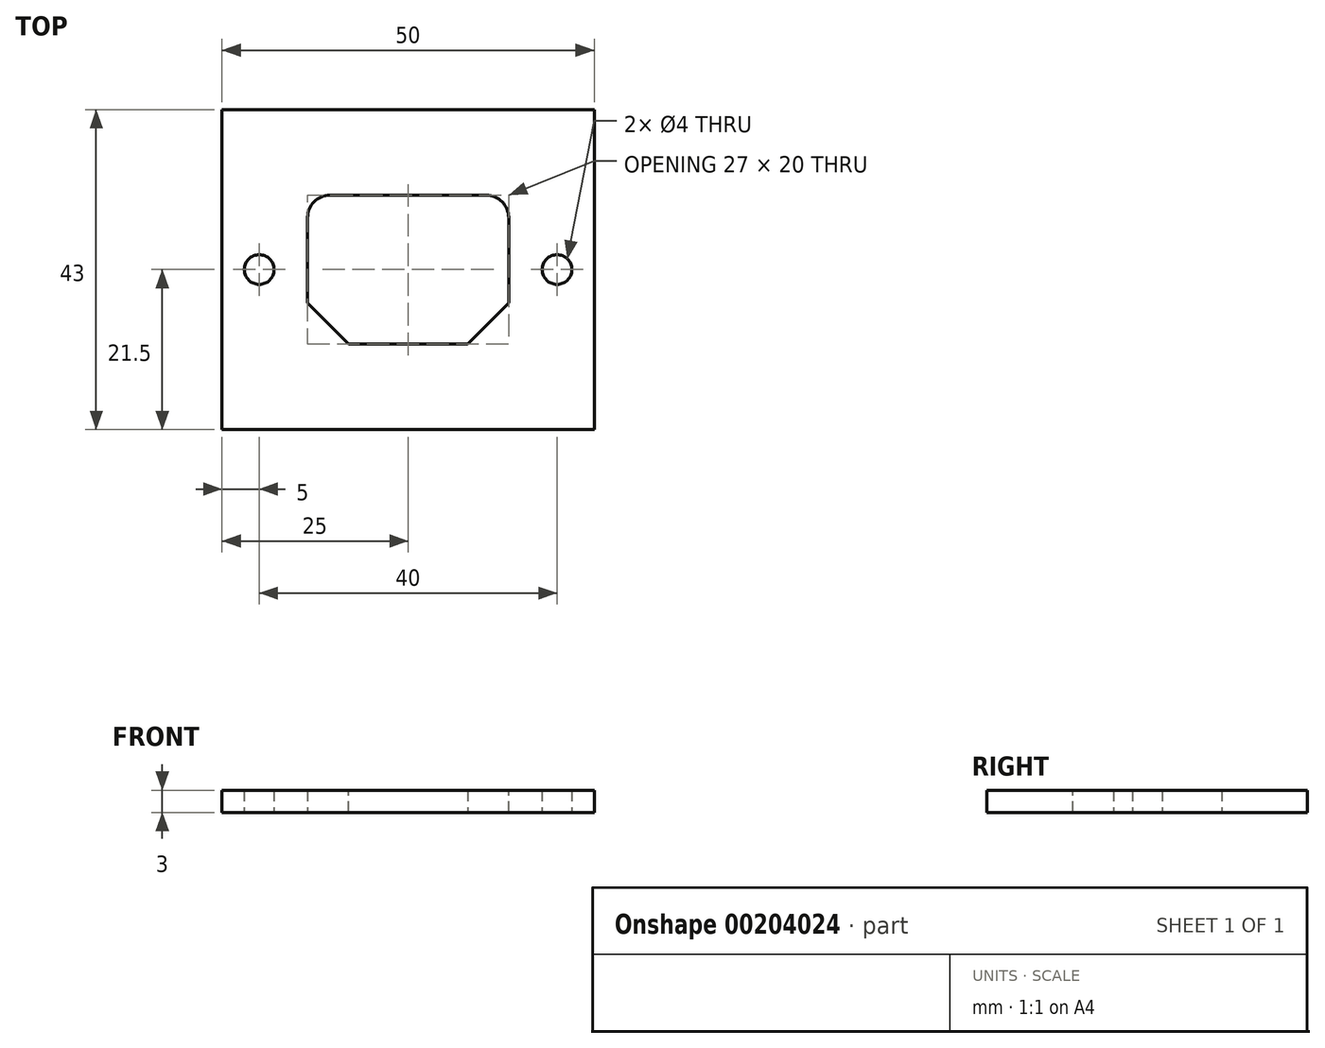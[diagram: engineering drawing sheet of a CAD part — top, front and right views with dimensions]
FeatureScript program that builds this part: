
annotation { "Feature Type Name" : "Feature", "Feature Type Description" : "" }
export const myFeature = defineFeature(function(context is Context, id is Id, definition is map)
    precondition{}
    {
        {
            var Q0;
            Q0=qCreatedBy(makeId("Top.planeOp"),FACE);
            var sketch = newSketch(context, id + "F0", { "sketchPlane" : qUnion([Q0])});
            skLineSegment(sketch, "E0", {"start": v(-13.5, -10) * mm, "end": v(13.5, -10) * mm});
            skLineSegment(sketch, "E1", {"start": v(13.5, -10) * mm, "end": v(13.5, 10) * mm});
            skLineSegment(sketch, "E2", {"start": v(13.5, 10) * mm, "end": v(-13.5, 10) * mm});
            skLineSegment(sketch, "E3", {"start": v(-13.5, 10) * mm, "end": v(-13.5, -10) * mm});
            skLineSegment(sketch, "E4.0", {"start": v(25, 21.5) * mm, "end": v(-25, 21.5) * mm});
            skLineSegment(sketch, "E4.1", {"start": v(25, -21.5) * mm, "end": v(25, 21.5) * mm});
            skLineSegment(sketch, "E4.2", {"start": v(-25, -21.5) * mm, "end": v(25, -21.5) * mm});
            skLineSegment(sketch, "E4.3", {"start": v(-25, 21.5) * mm, "end": v(-25, -21.5) * mm});
            skCircle(sketch, "E5", {"center": v(-20, 0) * mm, "radius": 2 * mm});
            skCircle(sketch, "E6", {"center": v(20, 0) * mm, "radius": 2 * mm});
            skSolve(sketch);
        }
        {
            var Q0;
            Q0=makeQuery(id+"F0.imprint","IMPRINT",FACE,{"disambiguationData":[TD([[makeQuery(id+"F0.imprint","IMPRINT",EDGE,{"derivedFrom":sQuery(id+"F0.wireOp",EDGE,"E0")}),-1.0]])]});
            extrude(context, id + "F1", {"entities" : qUnion([Q0]), "depth" : 3 * mm});
        }
        {
            var Q0;
            Q0=makeQuery(id+"F1.opExtrude","SWEPT_EDGE",EDGE,{"disambiguationData":[OSD([sQuery(id+"F0.wireOp",EDGE,"E2"),sQuery(id+"F0.wireOp",EDGE,"E3")])]});
            var Q1;
            Q1=makeQuery(id+"F1.opExtrude","SWEPT_EDGE",EDGE,{"disambiguationData":[OSD([sQuery(id+"F0.wireOp",EDGE,"E1"),sQuery(id+"F0.wireOp",EDGE,"E2")])]});
            fillet(context, id + "F2", {"entities" : qUnion([Q0, Q1]), "radius" : 3 * mm, "tangentPropagation" : true, "allowEdgeOverflow" : false});
        }
        {
            var Q0;
            Q0=makeQuery(id+"F1.opExtrude","SWEPT_EDGE",EDGE,{"disambiguationData":[OSD([sQuery(id+"F0.wireOp",EDGE,"E0"),sQuery(id+"F0.wireOp",EDGE,"E3")])]});
            var Q1;
            Q1=makeQuery(id+"F1.opExtrude","SWEPT_EDGE",EDGE,{"disambiguationData":[OSD([sQuery(id+"F0.wireOp",EDGE,"E0"),sQuery(id+"F0.wireOp",EDGE,"E1")])]});
            chamfer(context, id + "F3", {"entities" : qUnion([Q0, Q1]), "width" : 5.5 * mm, "tangentPropagation" : true});
        }
    });
